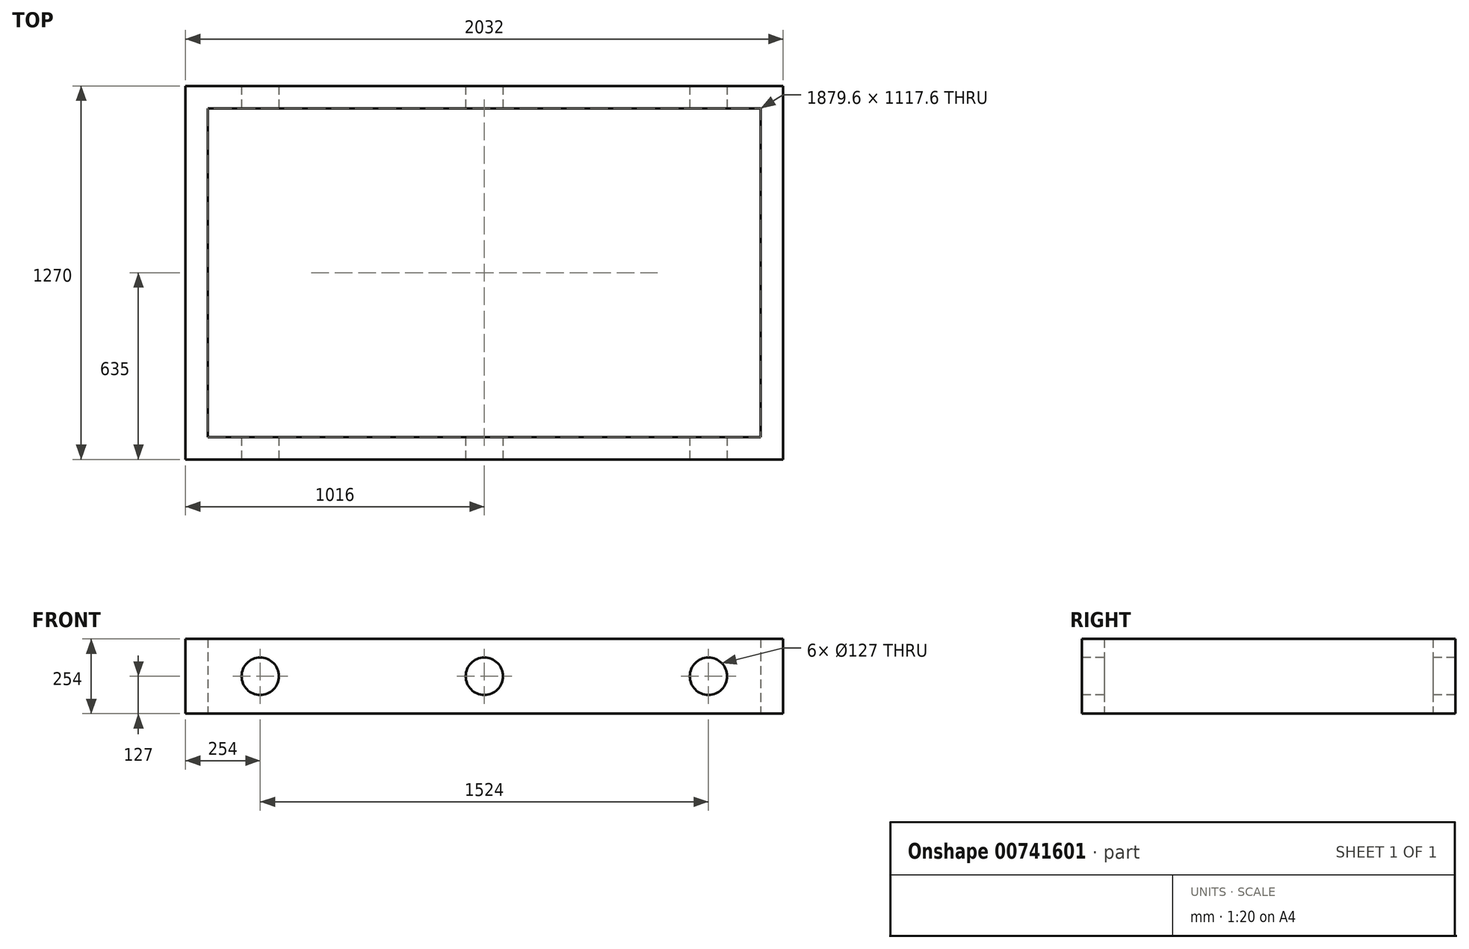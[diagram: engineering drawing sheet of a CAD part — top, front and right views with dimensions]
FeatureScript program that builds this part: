
annotation { "Feature Type Name" : "Feature", "Feature Type Description" : "" }
export const myFeature = defineFeature(function(context is Context, id is Id, definition is map)
    precondition{}
    {
        {
            var Q0;
            Q0=qCreatedBy(makeId("Top.planeOp"),FACE);
            var sketch = newSketch(context, id + "F0", { "sketchPlane" : qUnion([Q0])});
            skLineSegment(sketch, "E0.bottom", {"start": v(0, 0) * mm, "end": v(2032, 0) * mm});
            skLineSegment(sketch, "E0.top", {"start": v(0, 1270) * mm, "end": v(2032, 1270) * mm});
            skLineSegment(sketch, "E0.left", {"start": v(0, 0) * mm, "end": v(0, 1270) * mm});
            skLineSegment(sketch, "E0.right", {"start": v(2032, 0) * mm, "end": v(2032, 1270) * mm});
            skLineSegment(sketch, "E1.bottom", {"start": v(76.2, 1193.8) * mm, "end": v(1955.8, 1193.8) * mm});
            skLineSegment(sketch, "E1.top", {"start": v(76.2, 76.2) * mm, "end": v(1955.8, 76.2) * mm});
            skLineSegment(sketch, "E1.left", {"start": v(76.2, 1193.8) * mm, "end": v(76.2, 76.2) * mm});
            skLineSegment(sketch, "E1.right", {"start": v(1955.8, 1193.8) * mm, "end": v(1955.8, 76.2) * mm});
            skSolve(sketch);
        }
        {
            var Q0;
            Q0=makeQuery(id+"F0.imprint","IMPRINT",FACE,{"disambiguationData":[TD([[makeQuery(id+"F0.imprint","IMPRINT",EDGE,{"derivedFrom":sQuery(id+"F0.wireOp",EDGE,"E0.bottom")}),1.0]])]});
            extrude(context, id + "F1", {"entities" : qUnion([Q0]), "depth" : 254 * mm, "offsetDistance" : 25.4 * mm});
        }
        {
            var Q0;
            Q0=qCreatedBy(makeId("Front.planeOp"),FACE);
            var sketch = newSketch(context, id + "F2", { "sketchPlane" : qUnion([Q0])});
            skCircle(sketch, "E2", {"center": v(254, 127) * mm, "radius": 63.5 * mm});
            skCircle(sketch, "E3", {"center": v(1778, 127) * mm, "radius": 63.5 * mm});
            skCircle(sketch, "E4", {"center": v(1016, 127) * mm, "radius": 63.5 * mm});
            skSolve(sketch);
        }
        {
            var Q0;
            Q0=makeQuery(id+"F2.imprint","IMPRINT",FACE,{"disambiguationData":[TD([[makeQuery(id+"F2.imprint","IMPRINT",EDGE,{"derivedFrom":sQuery(id+"F2.wireOp",EDGE,"E3")}),1.0]])]});
            var Q1;
            Q1=makeQuery(id+"F2.imprint","IMPRINT",FACE,{"disambiguationData":[TD([[makeQuery(id+"F2.imprint","IMPRINT",EDGE,{"derivedFrom":sQuery(id+"F2.wireOp",EDGE,"E4")}),1.0]])]});
            var Q2;
            Q2=makeQuery(id+"F2.imprint","IMPRINT",FACE,{"disambiguationData":[TD([[makeQuery(id+"F2.imprint","IMPRINT",EDGE,{"derivedFrom":sQuery(id+"F2.wireOp",EDGE,"E2")}),1.0]])]});
            extrude(context, id + "F3", {"entities" : qUnion([Q0, Q1, Q2]), "operationType" : NewBodyOperationType.REMOVE, "endBound" : BoundingType.THROUGH_ALL, "oppositeDirection" : true, "depth" : 25.4 * mm, "offsetDistance" : 25.4 * mm});
        }
    });
